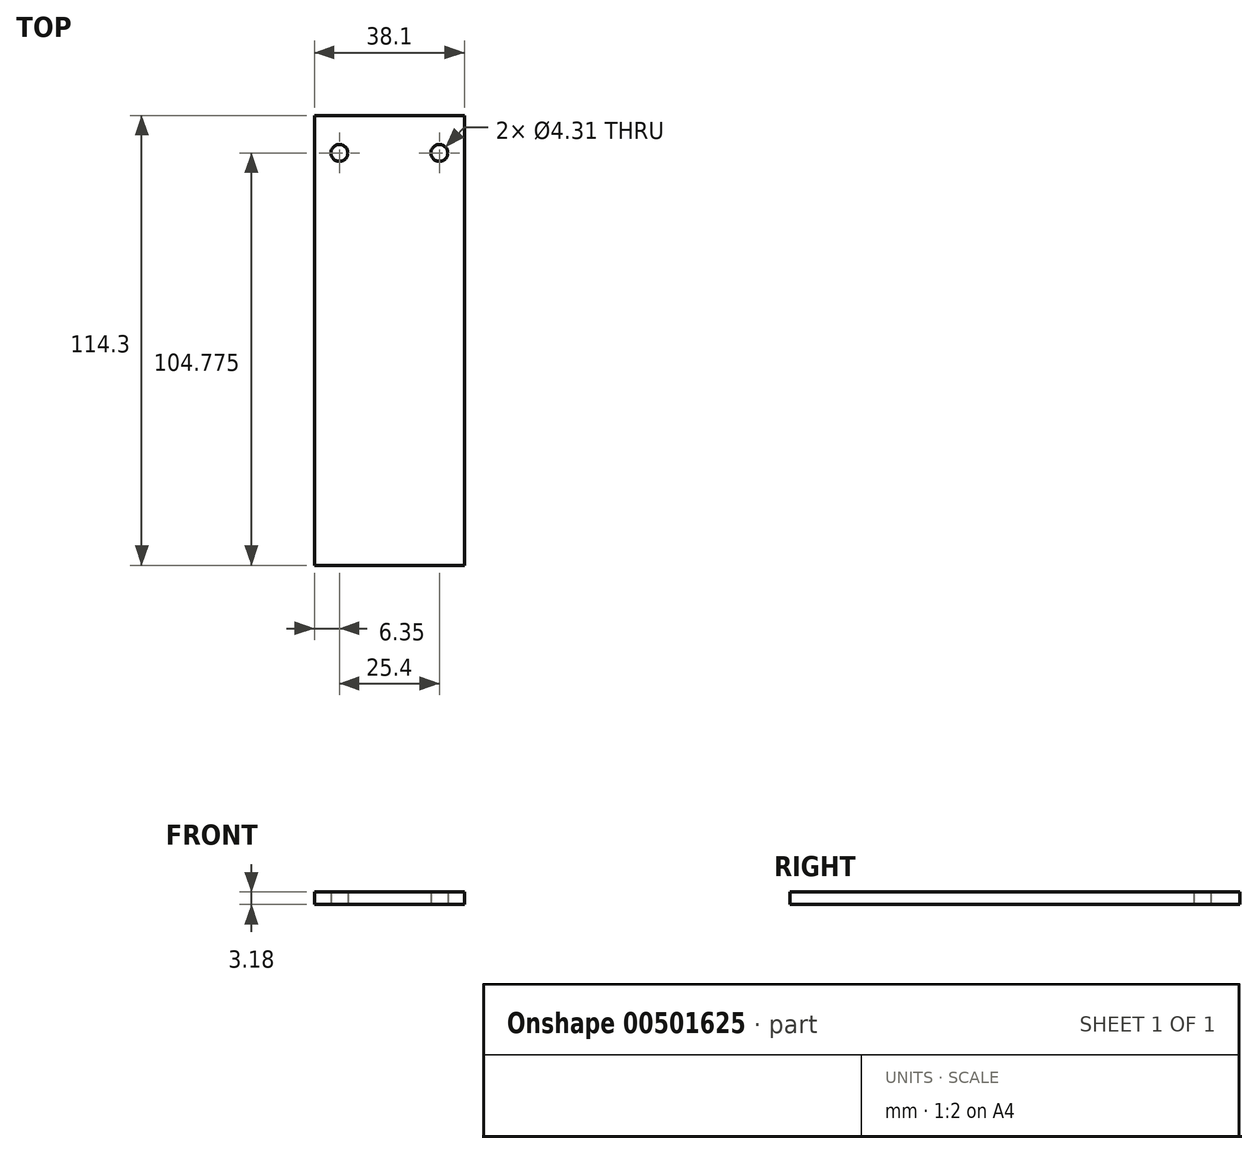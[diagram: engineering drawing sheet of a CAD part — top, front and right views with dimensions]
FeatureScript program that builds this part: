
annotation { "Feature Type Name" : "Feature", "Feature Type Description" : "" }
export const myFeature = defineFeature(function(context is Context, id is Id, definition is map)
    precondition{}
    {
        {
            var Q0;
            Q0=qCreatedBy(makeId("Top.planeOp"),FACE);
            var sketch = newSketch(context, id + "F0", { "sketchPlane" : qUnion([Q0])});
            skLineSegment(sketch, "E0.bottom", {"start": v(-19.05, 57.15) * mm, "end": v(19.05, 57.15) * mm});
            skLineSegment(sketch, "E0.top", {"start": v(-19.05, -57.15) * mm, "end": v(19.05, -57.15) * mm});
            skLineSegment(sketch, "E0.left", {"start": v(-19.05, 57.15) * mm, "end": v(-19.05, -57.15) * mm});
            skLineSegment(sketch, "E0.right", {"start": v(19.05, 57.15) * mm, "end": v(19.05, -57.15) * mm});
            skPoint(sketch, "E0.middle", {"position": v(0, 0) * mm});
            skCircle(sketch, "E1", {"center": v(-12.7, 47.62) * mm, "radius": 2.15 * mm});
            skCircle(sketch, "E2.MirrorC", {"center": v(12.7, 47.62) * mm, "radius": 2.15 * mm});
            skSolve(sketch);
        }
        {
            var Q0;
            Q0=makeQuery(id+"F0.imprint","IMPRINT",FACE,{"disambiguationData":[TD([[makeQuery(id+"F0.imprint","IMPRINT",EDGE,{"derivedFrom":sQuery(id+"F0.wireOp",EDGE,"E0.bottom")}),-1.0]])]});
            extrude(context, id + "F1", {"entities" : qUnion([Q0]), "depth" : 3.17 * mm});
        }
    });
